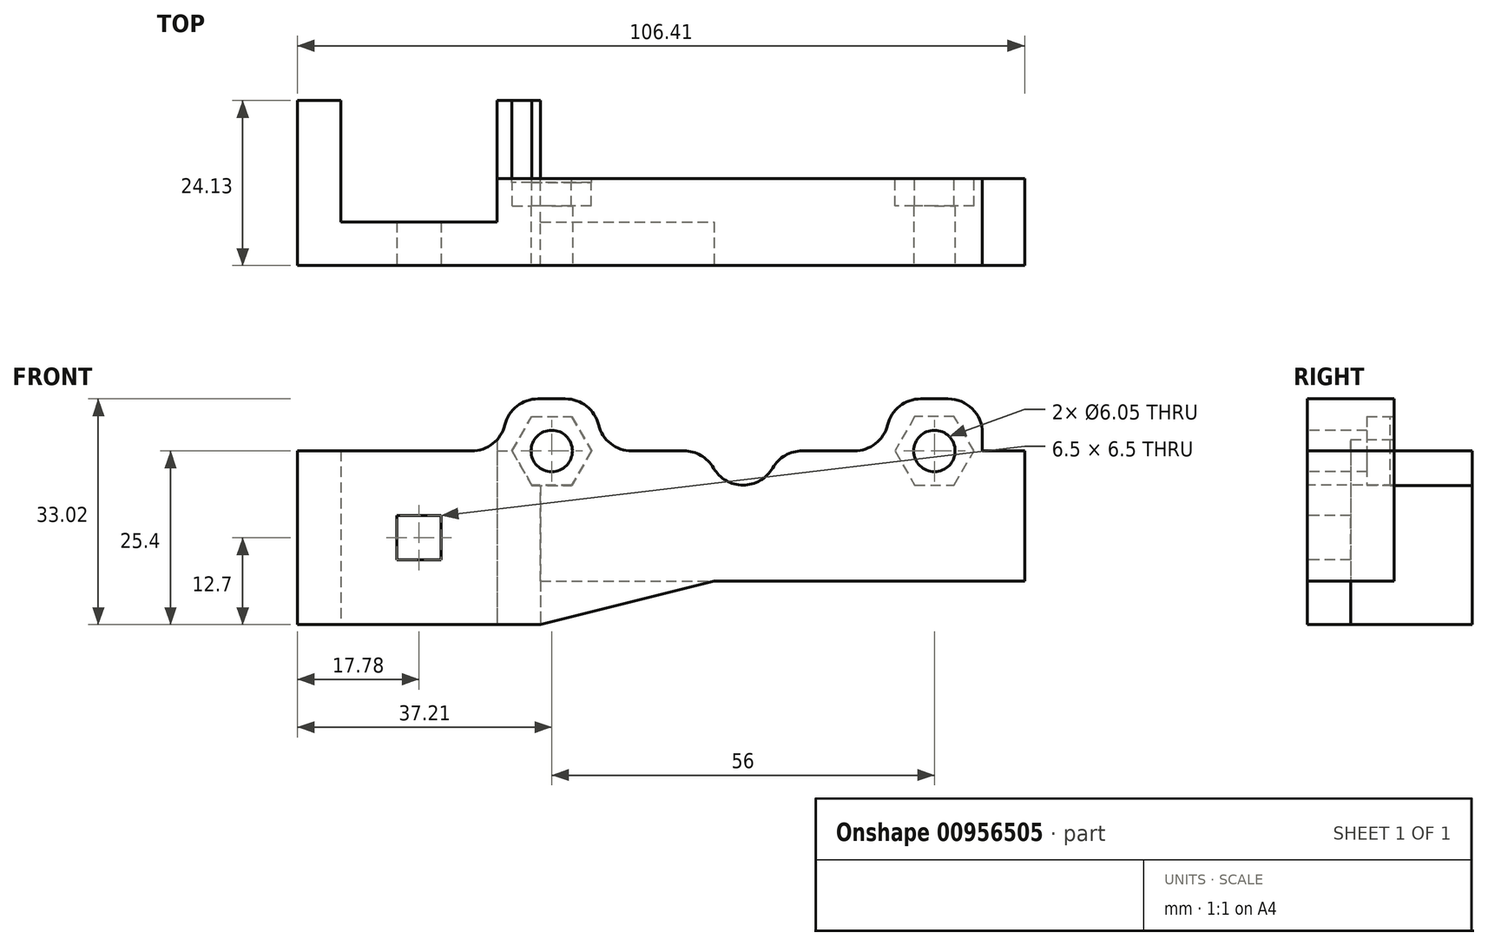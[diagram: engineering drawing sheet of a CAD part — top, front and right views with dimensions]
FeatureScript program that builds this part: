
annotation { "Feature Type Name" : "Feature", "Feature Type Description" : "" }
export const myFeature = defineFeature(function(context is Context, id is Id, definition is map)
    precondition{}
    {
        {
            var Q0;
            Q0=qCreatedBy(makeId("Top.planeOp"),FACE);
            var sketch = newSketch(context, id + "F0", { "sketchPlane" : qUnion([Q0])});
            skLineSegment(sketch, "E0.bottom", {"start": v(11.43, -9.78) * mm, "end": v(-11.43, -9.78) * mm});
            skLineSegment(sketch, "E0.left", {"start": v(11.43, -9.78) * mm, "end": v(11.43, 8) * mm});
            skLineSegment(sketch, "E0.right", {"start": v(-11.43, -9.78) * mm, "end": v(-11.43, 8) * mm});
            skPoint(sketch, "E0.middle", {"position": v(0, 0) * mm});
            skLineSegment(sketch, "E1.1", {"start": v(17.78, -16.13) * mm, "end": v(17.78, 8) * mm});
            skLineSegment(sketch, "E1.2", {"start": v(17.78, -16.13) * mm, "end": v(-17.78, -16.13) * mm});
            skLineSegment(sketch, "E1.3", {"start": v(-17.78, -16.13) * mm, "end": v(-17.78, 8) * mm});
            skLineSegment(sketch, "E2", {"start": v(-17.78, 8) * mm, "end": v(-17.78, -16.13) * mm});
            skLineSegment(sketch, "E3.bottom", {"start": v(-7.37, -9.78) * mm, "end": v(4.83, -9.78) * mm});
            skLineSegment(sketch, "E4", {"start": v(-17.78, 8) * mm, "end": v(-11.43, 8) * mm});
            skLineSegment(sketch, "E5", {"start": v(11.43, 8) * mm, "end": v(17.78, 8) * mm});
            skSolve(sketch);
        }
        {
            var Q0;
            Q0=makeQuery(id+"F0.imprint","IMPRINT",FACE,{"disambiguationData":[TD([[makeQuery(id+"F0.imprint","IMPRINT",EDGE,{"derivedFrom":sQuery(id+"F0.wireOp",EDGE,"E0.bottom")}),1.0]])]});
            var Q1;
            Q1=makeQuery(id+"F0.imprint","IMPRINT",FACE,{"disambiguationData":[TD([[makeQuery(id+"F0.imprint","IMPRINT",EDGE,{"derivedFrom":sQuery(id+"F0.wireOp",EDGE,"E3.bottom")}),1.0]])]});
            extrude(context, id + "F1", {"entities" : qUnion([Q0, Q1]), "endBound" : BoundingType.SYMMETRIC, "depth" : 25.4 * mm, "offsetDistance" : 25.4 * mm});
        }
        {
            var Q0;
            Q0=makeQuery(id+"F1.opExtrude","SWEPT_FACE",FACE,{"disambiguationData":[OSD([sQuery(id+"F0.wireOp",EDGE,"E1.2")])]});
            var sketch = newSketch(context, id + "F2", { "sketchPlane" : qUnion([Q0])});
            skCircle(sketch, "E6", {"center": v(0, 0) * mm, "radius": 3.25 * mm});
            skSolve(sketch);
        }
        {
            var Q0;
            Q0=makeQuery(id+"F2.imprint","IMPRINT",FACE,{"disambiguationData":[TD([[makeQuery(id+"F2.imprint","IMPRINT",EDGE,{"derivedFrom":sQuery(id+"F2.wireOp",EDGE,"E6")}),1.0]])]});
            extrude(context, id + "F3", {"entities" : qUnion([Q0]), "operationType" : NewBodyOperationType.REMOVE, "endBound" : BoundingType.THROUGH_ALL, "oppositeDirection" : true, "depth" : 25.4 * mm, "offsetDistance" : 25.4 * mm});
        }
        {
            var Q0;
            Q0=makeQuery(id+"F1.opExtrude","SWEPT_FACE",FACE,{"disambiguationData":[OSD([sQuery(id+"F0.wireOp",EDGE,"E1.2")])]});
            var sketch = newSketch(context, id + "F4", { "sketchPlane" : qUnion([Q0])});
            skLineSegment(sketch, "E7.bottom", {"start": v(3.25, -3.25) * mm, "end": v(-3.25, -3.25) * mm});
            skLineSegment(sketch, "E7.top", {"start": v(3.25, 3.25) * mm, "end": v(-3.25, 3.25) * mm});
            skLineSegment(sketch, "E7.left", {"start": v(3.25, -3.25) * mm, "end": v(3.25, 3.25) * mm});
            skLineSegment(sketch, "E7.right", {"start": v(-3.25, -3.25) * mm, "end": v(-3.25, 3.25) * mm});
            skPoint(sketch, "E7.middle", {"position": v(0, 0) * mm});
            skSolve(sketch);
        }
        {
            var Q0;
            Q0=qSketchRegion(id+"F4",true);
            extrude(context, id + "F5", {"entities" : qUnion([Q0]), "operationType" : NewBodyOperationType.REMOVE, "oppositeDirection" : true, "depth" : 7.62 * mm, "offsetDistance" : 25.4 * mm});
        }
        {
            var Q0;
            Q0=makeQuery(id+"F1.opExtrude","CAP_FACE",FACE,{"disambiguationData":[OSD([sQuery(id+"F0.wireOp",EDGE,"E0.bottom"),sQuery(id+"F0.wireOp",EDGE,"E0.top"),sQuery(id+"F0.wireOp",EDGE,"E0.left"),sQuery(id+"F0.wireOp",EDGE,"E0.right"),sQuery(id+"F0.wireOp",EDGE,"E1.0"),sQuery(id+"F0.wireOp",EDGE,"E1.1"),sQuery(id+"F0.wireOp",EDGE,"E1.2"),sQuery(id+"F0.wireOp",EDGE,"b5rAH07K-xdKy-zP9t-XWAS-kQrlMQJv2x7M.top"),sQuery(id+"F0.wireOp",EDGE,"b5rAH07K-xdKy-zP9t-XWAS-kQrlMQJv2x7M.left"),sQuery(id+"F0.wireOp",EDGE,"b5rAH07K-xdKy-zP9t-XWAS-kQrlMQJv2x7M.right"),sQuery(id+"F0.wireOp",EDGE,"fac62f1f-bd0c-4759-b51d-a7ef297a7c76.trimOffspring"),sQuery(id+"F0.wireOp",EDGE,"E2")])],"isStart":false});
            var sketch = newSketch(context, id + "F6", { "sketchPlane" : qUnion([Q0])});
            skLineSegment(sketch, "E8.bottom", {"start": v(17.78, -3.43) * mm, "end": v(88.63, -3.43) * mm});
            skLineSegment(sketch, "E8.top", {"start": v(17.78, -16.13) * mm, "end": v(88.63, -16.13) * mm});
            skLineSegment(sketch, "E8.left", {"start": v(17.78, -3.43) * mm, "end": v(17.78, -16.13) * mm});
            skLineSegment(sketch, "E8.right", {"start": v(88.63, -3.43) * mm, "end": v(88.63, -16.13) * mm});
            skSolve(sketch);
        }
        {
            var Q0;
            Q0=makeQuery(id+"F6.imprint","IMPRINT",FACE,{"disambiguationData":[TD([[makeQuery(id+"F6.imprint","IMPRINT",EDGE,{"derivedFrom":sQuery(id+"F6.wireOp",EDGE,"E8.bottom")}),-1.0]])]});
            extrude(context, id + "F7", {"entities" : qUnion([Q0]), "operationType" : NewBodyOperationType.ADD, "oppositeDirection" : true, "depth" : 19.05 * mm, "offsetDistance" : 25.4 * mm});
        }
        {
            var Q0;
            Q0=makeQuery(id+"F7.boolean.opBoolean","MERGE",FACE,{"derivedFrom":[makeQuery(id+"F1.opExtrude","SWEPT_FACE",FACE,{"disambiguationData":[OSD([sQuery(id+"F0.wireOp",EDGE,"E1.2")])]}),makeQuery(id+"F7.opExtrude","SWEPT_FACE",FACE,{"disambiguationData":[OSD([sQuery(id+"F6.wireOp",EDGE,"E8.top")])]})]});
            var sketch = newSketch(context, id + "F8", { "sketchPlane" : qUnion([Q0])});
            skLineSegment(sketch, "E9", {"start": v(17.78, -12.7) * mm, "end": v(17.78, -6.35) * mm});
            skLineSegment(sketch, "E10", {"start": v(17.78, -6.35) * mm, "end": v(43.18, -6.35) * mm});
            skLineSegment(sketch, "E11", {"start": v(43.18, -6.35) * mm, "end": v(17.78, -12.7) * mm});
            skSolve(sketch);
        }
        {
            var Q0;
            Q0=qSketchRegion(id+"F8",true);
            extrude(context, id + "F9", {"entities" : qUnion([Q0]), "operationType" : NewBodyOperationType.ADD, "oppositeDirection" : true, "depth" : 6.35 * mm, "offsetDistance" : 25.4 * mm});
        }
        {
            var Q0;
            Q0=makeQuery(id+"F7.boolean.opBoolean","MERGE",FACE,{"derivedFrom":[makeQuery(id+"F1.opExtrude","CAP_FACE",FACE,{"disambiguationData":[OSD([sQuery(id+"F0.wireOp",EDGE,"E0.bottom"),sQuery(id+"F0.wireOp",EDGE,"E0.top"),sQuery(id+"F0.wireOp",EDGE,"E0.left"),sQuery(id+"F0.wireOp",EDGE,"E0.right"),sQuery(id+"F0.wireOp",EDGE,"E1.0"),sQuery(id+"F0.wireOp",EDGE,"E1.1"),sQuery(id+"F0.wireOp",EDGE,"E1.2"),sQuery(id+"F0.wireOp",EDGE,"b5rAH07K-xdKy-zP9t-XWAS-kQrlMQJv2x7M.top"),sQuery(id+"F0.wireOp",EDGE,"b5rAH07K-xdKy-zP9t-XWAS-kQrlMQJv2x7M.left"),sQuery(id+"F0.wireOp",EDGE,"b5rAH07K-xdKy-zP9t-XWAS-kQrlMQJv2x7M.right"),sQuery(id+"F0.wireOp",EDGE,"fac62f1f-bd0c-4759-b51d-a7ef297a7c76.trimOffspring"),sQuery(id+"F0.wireOp",EDGE,"E2")])],"isStart":false}),makeQuery(id+"F7.opExtrude","CAP_FACE",FACE,{"disambiguationData":[OSD([sQuery(id+"F6.wireOp",EDGE,"E8.bottom"),sQuery(id+"F6.wireOp",EDGE,"E8.top"),sQuery(id+"F6.wireOp",EDGE,"E8.left"),sQuery(id+"F6.wireOp",EDGE,"E8.right")])],"isStart":true})]});
            var sketch = newSketch(context, id + "F10", { "sketchPlane" : qUnion([Q0])});
            skLineSegment(sketch, "E12.bottom", {"start": v(26.43, -16.13) * mm, "end": v(12.43, -16.13) * mm});
            skLineSegment(sketch, "E12.top", {"start": v(26.43, -3.43) * mm, "end": v(12.43, -3.43) * mm});
            skLineSegment(sketch, "E12.left", {"start": v(26.43, -16.13) * mm, "end": v(26.43, -3.43) * mm});
            skLineSegment(sketch, "E12.right", {"start": v(12.43, -16.13) * mm, "end": v(12.43, -3.43) * mm});
            skPoint(sketch, "E12.middle", {"position": v(19.43, -9.78) * mm});
            skLineSegment(sketch, "E13.bottom", {"start": v(82.43, -16.13) * mm, "end": v(68.43, -16.13) * mm});
            skLineSegment(sketch, "E13.top", {"start": v(82.43, -3.43) * mm, "end": v(68.43, -3.43) * mm});
            skLineSegment(sketch, "E13.left", {"start": v(82.43, -16.13) * mm, "end": v(82.43, -3.43) * mm});
            skLineSegment(sketch, "E13.right", {"start": v(68.43, -16.13) * mm, "end": v(68.43, -3.43) * mm});
            skPoint(sketch, "E13.middle", {"position": v(75.43, -9.78) * mm});
            skSolve(sketch);
        }
        {
            var Q0;
            Q0=qSketchRegion(id+"F10",true);
            extrude(context, id + "F11", {"entities" : qUnion([Q0]), "operationType" : NewBodyOperationType.ADD, "depth" : 7.62 * mm, "offsetDistance" : 25 * mm});
        }
        {
            var Q0;
            Q0=makeQuery(id+"F11.opExtrude","CAP_EDGE",EDGE,{"disambiguationData":[OSD([sQuery(id+"F10.wireOp",EDGE,"E12.left")])],"isStart":false});
            var Q1;
            Q1=makeQuery(id+"F11.opExtrude","CAP_EDGE",EDGE,{"disambiguationData":[OSD([sQuery(id+"F10.wireOp",EDGE,"E12.right")])],"isStart":false});
            var Q2;
            Q2=makeQuery(id+"F11.opExtrude","CAP_EDGE",EDGE,{"disambiguationData":[OSD([sQuery(id+"F10.wireOp",EDGE,"E13.right")])],"isStart":false});
            var Q3;
            Q3=makeQuery(id+"F11.opExtrude","CAP_EDGE",EDGE,{"disambiguationData":[OSD([sQuery(id+"F10.wireOp",EDGE,"E13.left")])],"isStart":false});
            fillet(context, id + "F12", {"entities" : qUnion([Q0, Q1, Q2, Q3]), "radius" : 5 * mm, "tangentPropagation" : true, "allowEdgeOverflow" : false});
        }
        {
            var Q0;
            Q0=makeQuery(id+"F11.boolean.opBoolean","MERGE",FACE,{"derivedFrom":[makeQuery(id+"F9.boolean.opBoolean","MERGE",FACE,{"derivedFrom":[makeQuery(id+"F7.boolean.opBoolean","MERGE",FACE,{"derivedFrom":[makeQuery(id+"F1.opExtrude","SWEPT_FACE",FACE,{"disambiguationData":[OSD([sQuery(id+"F0.wireOp",EDGE,"E1.2")])]}),makeQuery(id+"F7.opExtrude","SWEPT_FACE",FACE,{"disambiguationData":[OSD([sQuery(id+"F6.wireOp",EDGE,"E8.top")])]})]}),makeQuery(id+"F9.opExtrude","CAP_FACE",FACE,{"disambiguationData":[OSD([sQuery(id+"F8.wireOp",EDGE,"E9"),sQuery(id+"F8.wireOp",EDGE,"E10"),sQuery(id+"F8.wireOp",EDGE,"E11")])],"isStart":true})]}),makeQuery(id+"F11.opExtrude","SWEPT_FACE",FACE,{"disambiguationData":[OSD([sQuery(id+"F10.wireOp",EDGE,"E12.bottom")])]}),makeQuery(id+"F11.opExtrude","SWEPT_FACE",FACE,{"disambiguationData":[OSD([sQuery(id+"F10.wireOp",EDGE,"E13.bottom")])]})]});
            var sketch = newSketch(context, id + "F13", { "sketchPlane" : qUnion([Q0])});
            skCircle(sketch, "E14", {"center": v(19.43, 12.7) * mm, "radius": 3.02 * mm});
            skPoint(sketch, "E14.centerSnap0", {"position": v(19.43, 20.32) * mm});
            skCircle(sketch, "E15", {"center": v(75.43, 12.7) * mm, "radius": 3.02 * mm});
            skPoint(sketch, "E15.centerSnap0", {"position": v(75.43, 20.32) * mm});
            skSolve(sketch);
        }
        {
            var Q0;
            Q0=qSketchRegion(id+"F13",true);
            extrude(context, id + "F14", {"entities" : qUnion([Q0]), "operationType" : NewBodyOperationType.REMOVE, "endBound" : BoundingType.THROUGH_ALL, "oppositeDirection" : true, "depth" : 25 * mm, "offsetDistance" : 25 * mm});
        }
        {
            var Q0;
            Q0=makeQuery(id+"F11.boolean.opBoolean","MERGE",FACE,{"derivedFrom":[makeQuery(id+"F9.boolean.opBoolean","MERGE",FACE,{"derivedFrom":[makeQuery(id+"F7.boolean.opBoolean","MERGE",FACE,{"derivedFrom":[makeQuery(id+"F1.opExtrude","SWEPT_FACE",FACE,{"disambiguationData":[OSD([sQuery(id+"F0.wireOp",EDGE,"E1.2")])]}),makeQuery(id+"F7.opExtrude","SWEPT_FACE",FACE,{"disambiguationData":[OSD([sQuery(id+"F6.wireOp",EDGE,"E8.top")])]})]}),makeQuery(id+"F9.opExtrude","CAP_FACE",FACE,{"disambiguationData":[OSD([sQuery(id+"F8.wireOp",EDGE,"E9"),sQuery(id+"F8.wireOp",EDGE,"E10"),sQuery(id+"F8.wireOp",EDGE,"E11")])],"isStart":true})]}),makeQuery(id+"F11.opExtrude","SWEPT_FACE",FACE,{"disambiguationData":[OSD([sQuery(id+"F10.wireOp",EDGE,"E12.bottom")])]}),makeQuery(id+"F11.opExtrude","SWEPT_FACE",FACE,{"disambiguationData":[OSD([sQuery(id+"F10.wireOp",EDGE,"E13.bottom")])]})]});
            var sketch = newSketch(context, id + "F15", { "sketchPlane" : qUnion([Q0])});
            skCircle(sketch, "E16", {"center": v(47.43, 12.7) * mm, "radius": 5 * mm});
            skSolve(sketch);
        }
        {
            var Q0;
            Q0=qSketchRegion(id+"F15",true);
            extrude(context, id + "F16", {"entities" : qUnion([Q0]), "operationType" : NewBodyOperationType.REMOVE, "endBound" : BoundingType.THROUGH_ALL, "oppositeDirection" : true, "depth" : 25 * mm, "offsetDistance" : 25 * mm});
        }
        {
            var Q0;
            {var subQ0=sQuery(id+"F6.wireOp",EDGE,"E8.top");var subQ1=sQuery(id+"F6.wireOp",EDGE,"E8.bottom");var subQ2=sQuery(id+"F0.wireOp",EDGE,"E1.2");Q0=makeQuery(id+"F16.boolean.opBoolean","INTERSECT",EDGE,{"disambiguationData":[OD(0.0)],"derivedFrom":[makeQuery(id+"F11.boolean.opBoolean","SPLIT",FACE,{"disambiguationData":[TD([makeQuery(id+"F11.opExtrude","SWEPT_FACE",FACE,{"disambiguationData":[OSD([sQuery(id+"F10.wireOp",EDGE,"E12.left")])]})])],"derivedFrom":makeQuery(id+"F7.boolean.opBoolean","MERGE",FACE,{"derivedFrom":[makeQuery(id+"F1.opExtrude","CAP_FACE",FACE,{"disambiguationData":[OSD([sQuery(id+"F0.wireOp",EDGE,"E0.bottom"),sQuery(id+"F0.wireOp",EDGE,"E0.top"),sQuery(id+"F0.wireOp",EDGE,"E0.left"),sQuery(id+"F0.wireOp",EDGE,"E0.right"),sQuery(id+"F0.wireOp",EDGE,"E1.0"),sQuery(id+"F0.wireOp",EDGE,"E1.1"),subQ2,sQuery(id+"F0.wireOp",EDGE,"b5rAH07K-xdKy-zP9t-XWAS-kQrlMQJv2x7M.top"),sQuery(id+"F0.wireOp",EDGE,"b5rAH07K-xdKy-zP9t-XWAS-kQrlMQJv2x7M.left"),sQuery(id+"F0.wireOp",EDGE,"b5rAH07K-xdKy-zP9t-XWAS-kQrlMQJv2x7M.right"),sQuery(id+"F0.wireOp",EDGE,"fac62f1f-bd0c-4759-b51d-a7ef297a7c76.trimOffspring"),sQuery(id+"F0.wireOp",EDGE,"E2")])],"isStart":false}),makeQuery(id+"F7.opExtrude","CAP_FACE",FACE,{"disambiguationData":[OSD([subQ1,subQ0,sQuery(id+"F6.wireOp",EDGE,"E8.left"),sQuery(id+"F6.wireOp",EDGE,"E8.right")])],"isStart":true})]})}),makeQuery(id+"F16.opExtrude","SWEPT_FACE",FACE,{"disambiguationData":[OSD([sQuery(id+"F15.wireOp",EDGE,"E16")])]})]});}
            var Q1;
            {var subQ0=sQuery(id+"F6.wireOp",EDGE,"E8.top");var subQ1=sQuery(id+"F6.wireOp",EDGE,"E8.bottom");var subQ2=sQuery(id+"F0.wireOp",EDGE,"E1.2");Q1=makeQuery(id+"F16.boolean.opBoolean","INTERSECT",EDGE,{"disambiguationData":[OD(1.0)],"derivedFrom":[makeQuery(id+"F11.boolean.opBoolean","SPLIT",FACE,{"disambiguationData":[TD([makeQuery(id+"F11.opExtrude","SWEPT_FACE",FACE,{"disambiguationData":[OSD([sQuery(id+"F10.wireOp",EDGE,"E12.left")])]})])],"derivedFrom":makeQuery(id+"F7.boolean.opBoolean","MERGE",FACE,{"derivedFrom":[makeQuery(id+"F1.opExtrude","CAP_FACE",FACE,{"disambiguationData":[OSD([sQuery(id+"F0.wireOp",EDGE,"E0.bottom"),sQuery(id+"F0.wireOp",EDGE,"E0.top"),sQuery(id+"F0.wireOp",EDGE,"E0.left"),sQuery(id+"F0.wireOp",EDGE,"E0.right"),sQuery(id+"F0.wireOp",EDGE,"E1.0"),sQuery(id+"F0.wireOp",EDGE,"E1.1"),subQ2,sQuery(id+"F0.wireOp",EDGE,"b5rAH07K-xdKy-zP9t-XWAS-kQrlMQJv2x7M.top"),sQuery(id+"F0.wireOp",EDGE,"b5rAH07K-xdKy-zP9t-XWAS-kQrlMQJv2x7M.left"),sQuery(id+"F0.wireOp",EDGE,"b5rAH07K-xdKy-zP9t-XWAS-kQrlMQJv2x7M.right"),sQuery(id+"F0.wireOp",EDGE,"fac62f1f-bd0c-4759-b51d-a7ef297a7c76.trimOffspring"),sQuery(id+"F0.wireOp",EDGE,"E2")])],"isStart":false}),makeQuery(id+"F7.opExtrude","CAP_FACE",FACE,{"disambiguationData":[OSD([subQ1,subQ0,sQuery(id+"F6.wireOp",EDGE,"E8.left"),sQuery(id+"F6.wireOp",EDGE,"E8.right")])],"isStart":true})]})}),makeQuery(id+"F16.opExtrude","SWEPT_FACE",FACE,{"disambiguationData":[OSD([sQuery(id+"F15.wireOp",EDGE,"E16")])]})]});}
            fillet(context, id + "F17", {"entities" : qUnion([Q0, Q1]), "radius" : 5 * mm, "tangentPropagation" : true, "allowEdgeOverflow" : false});
        }
        {
            var Q0;
            Q0=makeQuery(id+"F11.boolean.opBoolean","MERGE",FACE,{"derivedFrom":[makeQuery(id+"F7.opExtrude","SWEPT_FACE",FACE,{"disambiguationData":[OSD([sQuery(id+"F6.wireOp",EDGE,"E8.bottom")])]}),makeQuery(id+"F11.opExtrude","SWEPT_FACE",FACE,{"disambiguationData":[OSD([sQuery(id+"F10.wireOp",EDGE,"E12.top")])]}),makeQuery(id+"F11.opExtrude","SWEPT_FACE",FACE,{"disambiguationData":[OSD([sQuery(id+"F10.wireOp",EDGE,"E13.top")])]})]});
            var sketch = newSketch(context, id + "F18", { "sketchPlane" : qUnion([Q0])});
            skCircle(sketch, "E17.cCircle", {"center": v(-75.43, 12.7) * mm, "radius": 5 * mm, "construction": true});
            skLineSegment(sketch, "E17.0", {"start": v(-72.54, 17.7) * mm, "end": v(-69.66, 12.7) * mm});
            skLineSegment(sketch, "E17.1", {"start": v(-69.66, 12.7) * mm, "end": v(-72.54, 7.7) * mm});
            skLineSegment(sketch, "E17.2", {"start": v(-72.54, 7.7) * mm, "end": v(-78.32, 7.7) * mm});
            skLineSegment(sketch, "E17.3", {"start": v(-78.32, 7.7) * mm, "end": v(-81.2, 12.7) * mm});
            skLineSegment(sketch, "E17.4", {"start": v(-81.2, 12.7) * mm, "end": v(-78.32, 17.7) * mm});
            skLineSegment(sketch, "E17.5", {"start": v(-78.32, 17.7) * mm, "end": v(-72.54, 17.7) * mm});
            skPoint(sketch, "E17.0.midPoint", {"position": v(-71.1, 15.2) * mm});
            skCircle(sketch, "E18.cCircle", {"center": v(-19.43, 12.7) * mm, "radius": 5 * mm, "construction": true});
            skLineSegment(sketch, "E18.0", {"start": v(-22.32, 7.7) * mm, "end": v(-25.2, 12.7) * mm});
            skLineSegment(sketch, "E18.1", {"start": v(-25.2, 12.7) * mm, "end": v(-22.32, 17.7) * mm});
            skLineSegment(sketch, "E18.2", {"start": v(-22.32, 17.7) * mm, "end": v(-16.54, 17.7) * mm});
            skLineSegment(sketch, "E18.3", {"start": v(-16.54, 17.7) * mm, "end": v(-13.66, 12.7) * mm});
            skLineSegment(sketch, "E18.4", {"start": v(-13.66, 12.7) * mm, "end": v(-16.54, 7.7) * mm});
            skLineSegment(sketch, "E18.5", {"start": v(-16.54, 7.7) * mm, "end": v(-22.32, 7.7) * mm});
            skPoint(sketch, "E18.0.midPoint", {"position": v(-23.76, 10.2) * mm});
            skSolve(sketch);
        }
        {
            var Q0;
            Q0=qSketchRegion(id+"F18",true);
            extrude(context, id + "F19", {"entities" : qUnion([Q0]), "operationType" : NewBodyOperationType.REMOVE, "oppositeDirection" : true, "depth" : 4 * mm, "offsetDistance" : 25 * mm});
        }
        {
            var Q0;
            Q0=makeQuery(id+"F11.opExtrude","CAP_EDGE",EDGE,{"disambiguationData":[OSD([sQuery(id+"F10.wireOp",EDGE,"E13.left")])],"isStart":true});
            var Q1;
            Q1=makeQuery(id+"F11.opExtrude","CAP_EDGE",EDGE,{"disambiguationData":[OSD([sQuery(id+"F10.wireOp",EDGE,"E13.right")])],"isStart":true});
            var Q2;
            Q2=makeQuery(id+"F11.opExtrude","CAP_EDGE",EDGE,{"disambiguationData":[OSD([sQuery(id+"F10.wireOp",EDGE,"E12.left")])],"isStart":true});
            var Q3;
            Q3=makeQuery(id+"F11.opExtrude","CAP_EDGE",EDGE,{"disambiguationData":[OSD([sQuery(id+"F10.wireOp",EDGE,"E12.right")])],"isStart":true});
            fillet(context, id + "F20", {"entities" : qUnion([Q0, Q1, Q2, Q3]), "radius" : 5 * mm, "tangentPropagation" : true, "allowEdgeOverflow" : false});
        }
        {
            var Q0;
            Q0=makeQuery(id+"F1.opExtrude","SWEPT_FACE",FACE,{"disambiguationData":[OSD([sQuery(id+"F0.wireOp",EDGE,"E5")])]});
            var sketch = newSketch(context, id + "F21", { "sketchPlane" : qUnion([Q0])});
            skCircle(sketch, "E19.cCircle", {"center": v(-19.43, 12.7) * mm, "radius": 5.05 * mm, "construction": true});
            skLineSegment(sketch, "E19.0", {"start": v(-16.51, 7.65) * mm, "end": v(-22.35, 7.65) * mm});
            skLineSegment(sketch, "E19.1", {"start": v(-22.35, 7.65) * mm, "end": v(-25.26, 12.7) * mm});
            skLineSegment(sketch, "E19.2", {"start": v(-25.26, 12.7) * mm, "end": v(-22.35, 17.75) * mm});
            skLineSegment(sketch, "E19.3", {"start": v(-22.35, 17.75) * mm, "end": v(-16.51, 17.75) * mm});
            skLineSegment(sketch, "E19.4", {"start": v(-16.51, 17.75) * mm, "end": v(-13.6, 12.7) * mm});
            skLineSegment(sketch, "E19.5", {"start": v(-13.6, 12.7) * mm, "end": v(-16.51, 7.65) * mm});
            skPoint(sketch, "E19.0.midPoint", {"position": v(-19.43, 7.65) * mm});
            skSolve(sketch);
        }
        {
            var Q0;
            Q0=qSketchRegion(id+"F21",true);
            extrude(context, id + "F22", {"entities" : qUnion([Q0]), "operationType" : NewBodyOperationType.REMOVE, "oppositeDirection" : true, "depth" : 12 * mm, "offsetDistance" : 25 * mm});
        }
    });
